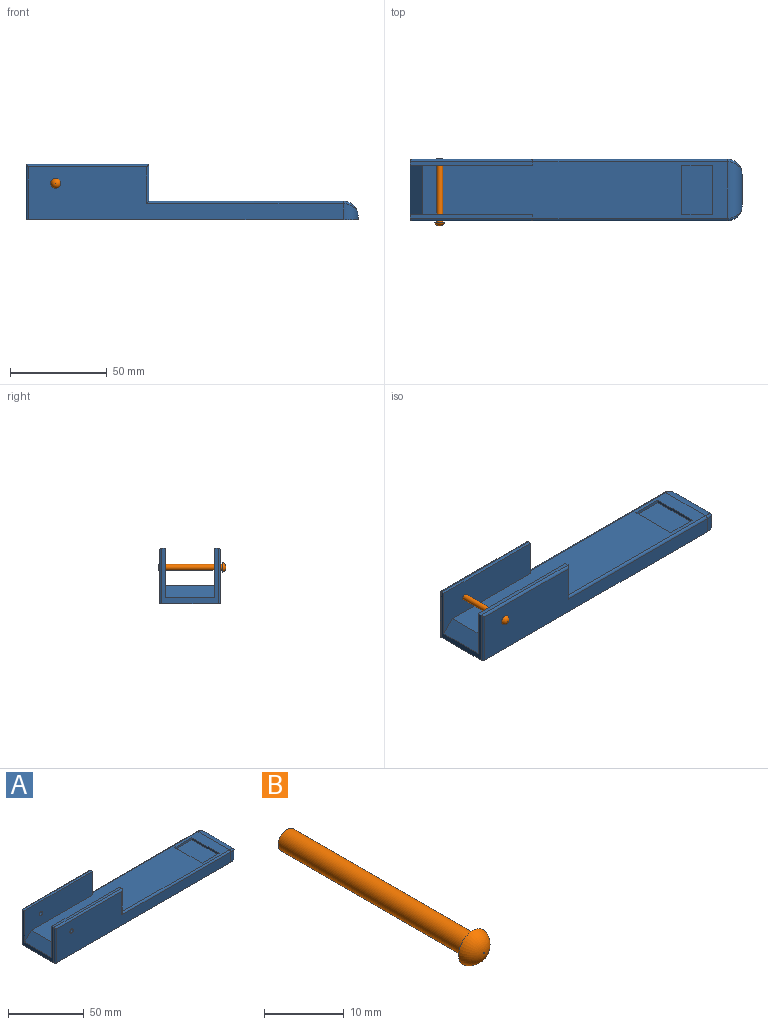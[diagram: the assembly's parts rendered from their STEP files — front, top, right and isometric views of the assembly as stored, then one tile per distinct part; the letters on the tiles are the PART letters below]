
ASSEMBLY  parts=2 mates=1
PART A: 33 faces, bbox 171.5x31.8x28.6 mm
  f0: plane 157.48x29.21mm, normal (0,0,1), area 3979mm2, adj f6,f7,f9,f10,f12,f13,f16,f17
  f1: plane 162.56x27.31mm, normal (0,1,0), area 2495.3mm2, adj f5,f13,f15,f25,f26,f27,f32
  f2: plane 29.21x28.58mm, normal (-1,0,0), area 189.5mm2, adj f5,f7,f8,f10,f11,f21,f22,f25
  f3: plane 162.56x27.31mm, normal (0,-1,0), area 2495.3mm2, adj f5,f12,f14,f22,f23,f24,f28
  f4: plane 16.51x1.91mm, normal (1,0,0), area 31.5mm2, adj f5,f28,f30,f32
  f5: plane 171.45x31.75mm, normal (0,0,-1), area 5417.9mm2, adj f1,f2,f3,f4,f22,f25,f28,f32
  f6: plane 19.05x1.91mm, normal (1,0,0), area 36.3mm2, adj f0,f7,f8,f27
  f7: plane 63.5x25.4mm, normal (0,-1,0), area 1221.9mm2, adj f0,f2,f6,f8,f15,f21
  f8: plane 63.5x1.91mm, normal (0,0,1), area 121mm2, adj f2,f6,f7,f26
  f9: plane 19.05x1.91mm, normal (1,0,0), area 36.3mm2, adj f0,f10,f11,f24
  f10: plane 63.5x25.4mm, normal (0,1,0), area 1221.9mm2, adj f0,f2,f9,f11,f14,f21
  f11: plane 63.5x1.91mm, normal (0,0,1), area 121mm2, adj f2,f9,f10,f23
  f12: cylinder r=1.27mm len=101.6mm, axis (1,0,0), area 201.1mm2, adj f0,f3,f24,f29
  f13: cylinder r=1.27mm len=101.6mm, axis (-1,0,0), area 201.1mm2, adj f0,f1,f27,f31
  f14: cylinder r=1.59mm len=3.18mm, axis (0,1,0), area 31.7mm2, adj f3,f10
  f15: cylinder r=1.59mm len=3.18mm, axis (0,1,0), area 31.7mm2, adj f1,f7
  f16: plane 25.4x1.6mm, normal (1,0,0), area 40.6mm2, adj f0,f17,f19,f20
  f17: plane 15.88x1.6mm, normal (0,1,0), area 25.4mm2, adj f0,f16,f18,f20
  f18: plane 25.4x1.6mm, normal (-1,0,0), area 40.6mm2, adj f0,f17,f19,f20
  f19: plane 15.88x1.6mm, normal (0,-1,0), area 25.4mm2, adj f0,f16,f18,f20
  f20: plane 25.4x15.88mm, normal (0,0,1), area 403.2mm2, adj f16,f17,f18,f19
  f21: plane 25.4x6.35mm, normal (-0.71,0,0.71), area 228.1mm2, adj f0,f2,f7,f10
  f22: cylinder r=1.27mm len=28.58mm, axis (0,0,1), area 56.1mm2, adj f2,f3,f5,f23
  f23: cylinder r=1.27mm len=63.5mm, axis (1,0,0), area 124.8mm2, adj f3,f11,f22,f24
  f24: cylinder r=1.27mm len=20.32mm, axis (0,0,-1), area 38mm2, adj f3,f9,f12,f23
  f25: cylinder r=1.27mm len=28.58mm, axis (0,0,-1), area 56.1mm2, adj f1,f2,f5,f26
  f26: cylinder r=1.27mm len=63.5mm, axis (1,0,0), area 124.8mm2, adj f1,f8,f25,f27
  f27: cylinder r=1.27mm len=20.32mm, axis (0,0,-1), area 38mm2, adj f1,f6,f13,f26
  f28: cylinder r=7.62mm len=8.26mm, axis (0,0,-1), area 71.2mm2, adj f3,f4,f5,f29
  f29: bspline ~7.91x7.62mm, area 16.5mm2, adj f12,f28,f30
  f30: cylinder r=7.62mm len=29.21mm, axis (0,1,0), area 294.4mm2, adj f0,f4,f29,f31
  f31: bspline ~8.78x7.62mm, area 16.5mm2, adj f13,f30,f32
  f32: cylinder r=7.62mm len=8.26mm, axis (0,0,1), area 71.2mm2, adj f1,f4,f5,f31
PART B: 5 faces, bbox 5.1x34.9x5.1 mm
  f0: cylinder r=1.56mm len=33.02mm, axis (0,1,0), area 324.1mm2, adj f1,f3
  f1: plane 3.12x3.12mm, normal (0,1,0), area 7.7mm2, adj f0
  f2: plane 0.16x0.16mm, normal (0,-1,0), area 0mm2, adj f4
  f3: plane 5.08x5.08mm, normal (0,1,0), area 12.6mm2, adj f0,f4
  f4: torus R=0.08mm, axis (0,1,0), area 32.1mm2, adj f2,f3
PLACE A t=(27.86,-88.7,-28.69)mm
PLACE B t=(-18.86,-48.86,-25.79)mm
MATE slider A.f14 <-> B.f0  axis (0,-1,0) through (-8.67,-81.15,-19.45)mm
